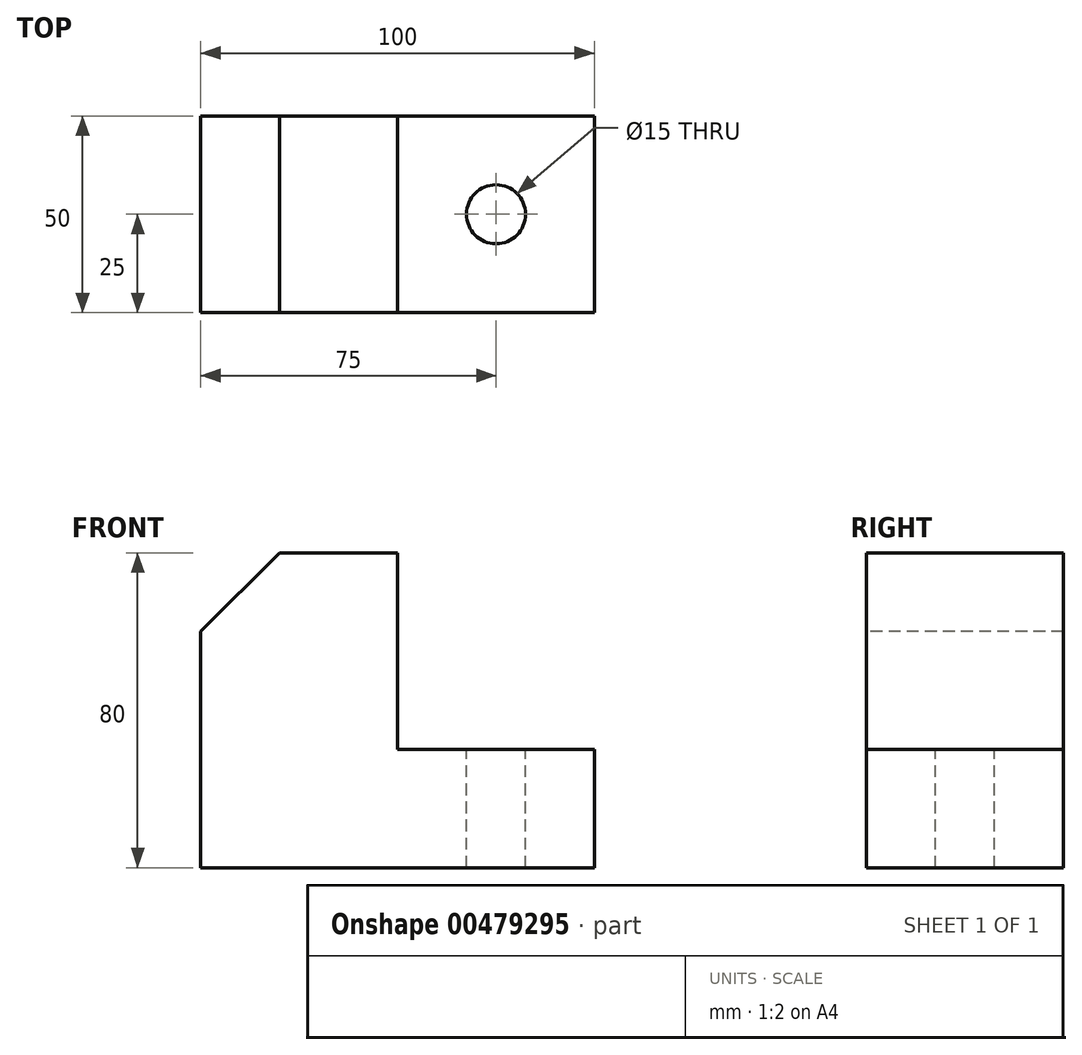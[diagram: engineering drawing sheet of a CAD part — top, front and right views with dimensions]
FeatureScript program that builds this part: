
annotation { "Feature Type Name" : "Feature", "Feature Type Description" : "" }
export const myFeature = defineFeature(function(context is Context, id is Id, definition is map)
    precondition{}
    {
        {
            var Q0;
            Q0=qCreatedBy(makeId("Top.planeOp"),FACE);
            var sketch = newSketch(context, id + "F0", { "sketchPlane" : qUnion([Q0])});
            skLineSegment(sketch, "E0.bottom", {"start": v(0, 0) * mm, "end": v(100, 0) * mm});
            skLineSegment(sketch, "E0.top", {"start": v(0, 50) * mm, "end": v(100, 50) * mm});
            skLineSegment(sketch, "E0.left", {"start": v(0, 0) * mm, "end": v(0, 50) * mm});
            skLineSegment(sketch, "E0.right", {"start": v(100, 0) * mm, "end": v(100, 50) * mm});
            skSolve(sketch);
        }
        {
            var Q0;
            Q0=makeQuery(id+"F0.imprint","IMPRINT",FACE,{"disambiguationData":[TD([[makeQuery(id+"F0.imprint","IMPRINT",EDGE,{"derivedFrom":sQuery(id+"F0.wireOp",EDGE,"E0.bottom")}),1.0]])]});
            extrude(context, id + "F1", {"entities" : qUnion([Q0]), "depth" : 30 * mm});
        }
        {
            var Q0;
            Q0=makeQuery(id+"F1.opExtrude","CAP_FACE",FACE,{"disambiguationData":[OSD([sQuery(id+"F0.wireOp",EDGE,"E0.bottom"),sQuery(id+"F0.wireOp",EDGE,"E0.top"),sQuery(id+"F0.wireOp",EDGE,"E0.left"),sQuery(id+"F0.wireOp",EDGE,"E0.right")])],"isStart":false});
            var sketch = newSketch(context, id + "F2", { "sketchPlane" : qUnion([Q0])});
            skLineSegment(sketch, "E1.bottom", {"start": v(0, 0) * mm, "end": v(50, 0) * mm});
            skLineSegment(sketch, "E1.top", {"start": v(0, 50) * mm, "end": v(50, 50) * mm});
            skLineSegment(sketch, "E1.left", {"start": v(0, 0) * mm, "end": v(0, 50) * mm});
            skLineSegment(sketch, "E1.right", {"start": v(50, 0) * mm, "end": v(50, 50) * mm});
            skSolve(sketch);
        }
        {
            var Q0;
            Q0 = qSketchRegion(id + "F2", true);
            extrude(context, id + "F3", {"entities" : qUnion([Q0]), "operationType" : NewBodyOperationType.ADD, "depth" : 50 * mm});
        }
        {
            var Q0;
            Q0=makeQuery(id+"F3.boolean.opBoolean","MERGE",FACE,{"derivedFrom":[makeQuery(id+"F1.opExtrude","SWEPT_FACE",FACE,{"disambiguationData":[OSD([sQuery(id+"F0.wireOp",EDGE,"E0.bottom")])]}),makeQuery(id+"F3.opExtrude","SWEPT_FACE",FACE,{"disambiguationData":[OSD([sQuery(id+"F2.wireOp",EDGE,"E1.bottom")])]})]});
            var sketch = newSketch(context, id + "F4", { "sketchPlane" : qUnion([Q0])});
            skLineSegment(sketch, "E2.bottom", {"start": v(0, 80) * mm, "end": v(20, 80) * mm});
            skLineSegment(sketch, "E2.top", {"start": v(0, 60) * mm, "end": v(20, 60) * mm});
            skLineSegment(sketch, "E2.left", {"start": v(0, 80) * mm, "end": v(0, 60) * mm});
            skLineSegment(sketch, "E2.right", {"start": v(20, 80) * mm, "end": v(20, 60) * mm});
            skLineSegment(sketch, "E3", {"start": v(20, 80) * mm, "end": v(0, 60) * mm});
            skSolve(sketch);
        }
        {
            var Q0;
            Q0=makeQuery(id+"F4.imprint","IMPRINT",FACE,{"disambiguationData":[TD([[makeQuery(id+"F4.imprint","IMPRINT",EDGE,{"derivedFrom":sQuery(id+"F4.wireOp",EDGE,"E2.bottom")}),-1.0]])]});
            extrude(context, id + "F5", {"entities" : qUnion([Q0]), "operationType" : NewBodyOperationType.REMOVE, "endBound" : BoundingType.THROUGH_ALL, "oppositeDirection" : true, "depth" : 25 * mm});
        }
        {
            var Q0;
            Q0=makeQuery(id+"F1.opExtrude","CAP_FACE",FACE,{"disambiguationData":[OSD([sQuery(id+"F0.wireOp",EDGE,"E0.bottom"),sQuery(id+"F0.wireOp",EDGE,"E0.top"),sQuery(id+"F0.wireOp",EDGE,"E0.left"),sQuery(id+"F0.wireOp",EDGE,"E0.right")])],"isStart":false});
            var sketch = newSketch(context, id + "F6", { "sketchPlane" : qUnion([Q0])});
            skCircle(sketch, "E4", {"center": v(75, 25) * mm, "radius": 7.5 * mm});
            skSolve(sketch);
        }
        {
            var Q0;
            Q0=makeQuery(id+"F6.imprint","IMPRINT",FACE,{"disambiguationData":[TD([[makeQuery(id+"F6.imprint","IMPRINT",EDGE,{"derivedFrom":sQuery(id+"F6.wireOp",EDGE,"E4")}),1.0]])]});
            extrude(context, id + "F7", {"entities" : qUnion([Q0]), "operationType" : NewBodyOperationType.REMOVE, "endBound" : BoundingType.THROUGH_ALL, "oppositeDirection" : true, "depth" : 25 * mm});
        }
    });
